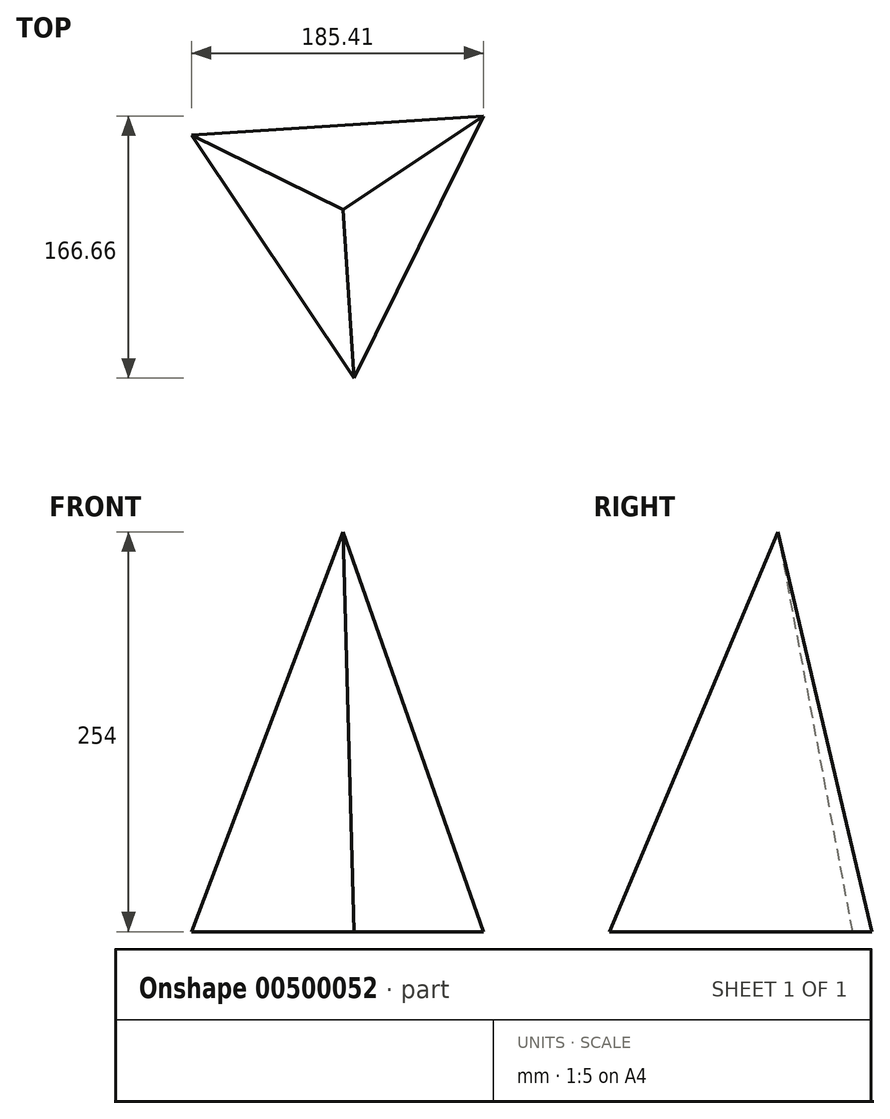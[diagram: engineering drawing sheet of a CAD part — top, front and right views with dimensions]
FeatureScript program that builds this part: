
annotation { "Feature Type Name" : "Feature", "Feature Type Description" : "" }
export const myFeature = defineFeature(function(context is Context, id is Id, definition is map)
    precondition{}
    {
        {
            var Q0;
            Q0=qCreatedBy(makeId("Top.planeOp"),FACE);
            var sketch = newSketch(context, id + "F0", { "sketchPlane" : qUnion([Q0])});
            skCircle(sketch, "E0.cCircle", {"center": v(0, 0) * mm, "radius": 107.28 * mm, "construction": true});
            skLineSegment(sketch, "E0.0", {"start": v(89.2, 59.6) * mm, "end": v(7.03, -107.05) * mm});
            skLineSegment(sketch, "E0.1", {"start": v(7.03, -107.05) * mm, "end": v(-96.22, 47.44) * mm});
            skLineSegment(sketch, "E0.2", {"start": v(-96.22, 47.44) * mm, "end": v(89.2, 59.6) * mm});
            skSolve(sketch);
        }
        {
            var Q0;
            Q0=qCreatedBy(makeId("Top.planeOp"),FACE);
            cPlane(context, id + "F1", {"entities" : qUnion([Q0]), "cplaneType" : CPlaneType.OFFSET, "offset" : 254 * mm, "width" : 152.4 * mm, "height" : 152.4 * mm});
        }
        {
            var Q0;
            Q0=qCreatedBy(id+"F1.planeOp",FACE);
            var sketch = newSketch(context, id + "F2", { "sketchPlane" : qUnion([Q0])});
            skPoint(sketch, "E1", {"position": v(0, 0) * mm});
            skSolve(sketch);
        }
        {
            var Q0;
            Q0=makeQuery(id+"F0.imprint","IMPRINT",FACE,{"disambiguationData":[TD([[makeQuery(id+"F0.imprint","IMPRINT",EDGE,{"derivedFrom":sQuery(id+"F0.wireOp",EDGE,"E0.0")}),-1.0]])]});
            var Q1;
            Q1=sQuery(id+"F2.wireOp",VERTEX,"E1");
            loft(context, id + "F3", {"sheetProfilesArray" : [{ "sheetProfileEntities" : qUnion([Q0]) }, { "sheetProfileEntities" : qUnion([Q1]) }]});
        }
    });
